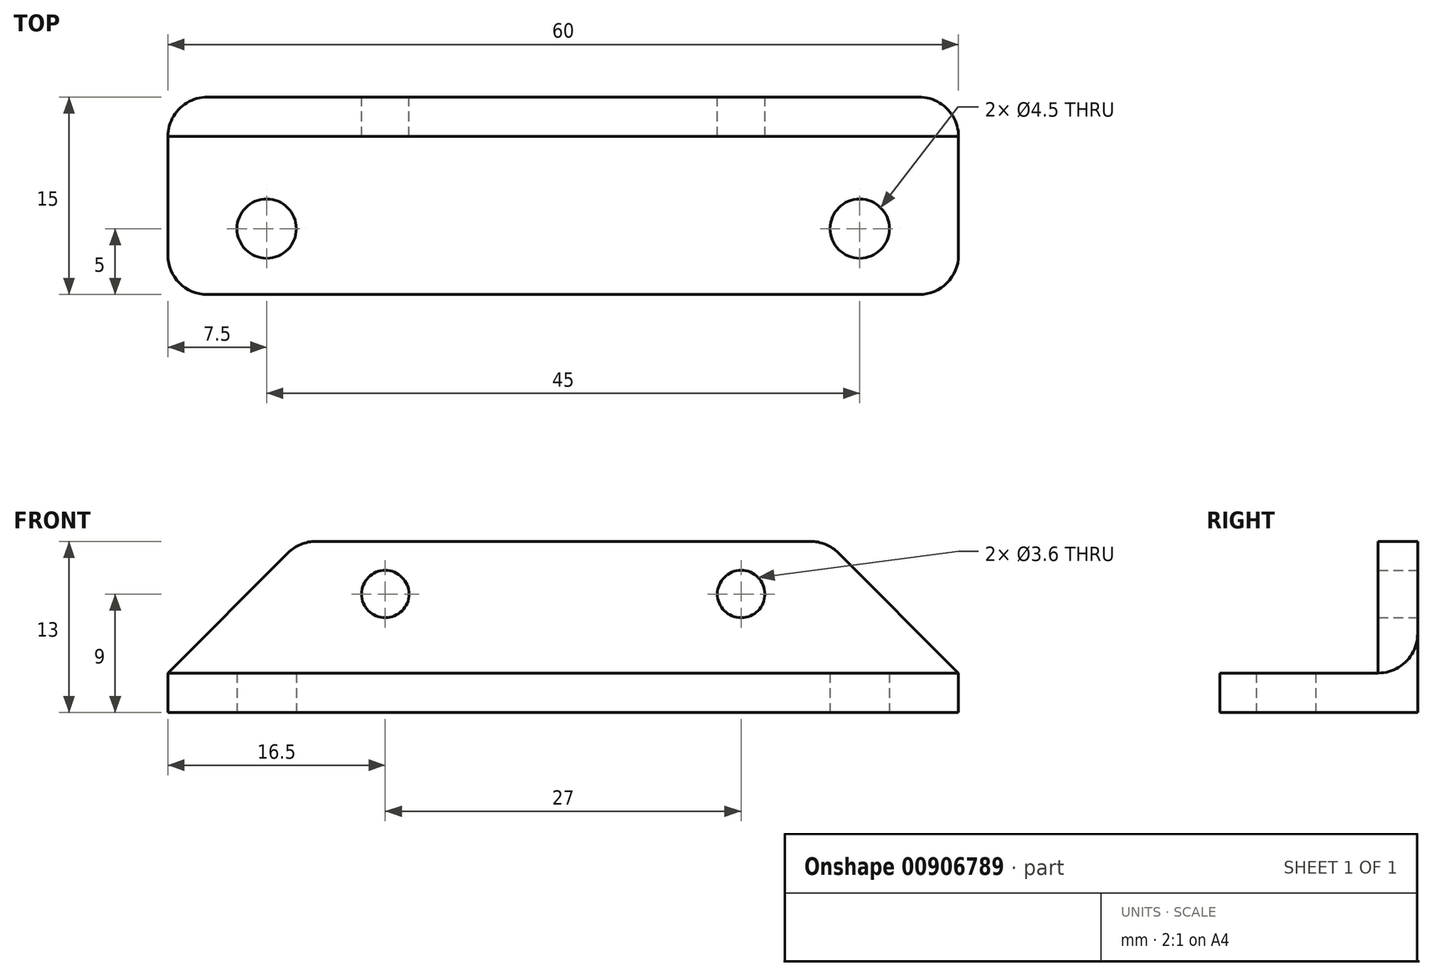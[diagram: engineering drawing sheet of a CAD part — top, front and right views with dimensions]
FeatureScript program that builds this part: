
annotation { "Feature Type Name" : "Feature", "Feature Type Description" : "" }
export const myFeature = defineFeature(function(context is Context, id is Id, definition is map)
    precondition{}
    {
        {
            var Q0;
            Q0=qCreatedBy(makeId("Top.planeOp"),FACE);
            var sketch = newSketch(context, id + "F0", { "sketchPlane" : qUnion([Q0])});
            skLineSegment(sketch, "E0.bottom", {"start": v(50, -10) * mm, "end": v(-50, -10) * mm, "construction": true});
            skLineSegment(sketch, "E0.top", {"start": v(50, 10) * mm, "end": v(-50, 10) * mm, "construction": true});
            skLineSegment(sketch, "E0.left", {"start": v(50, -10) * mm, "end": v(50, 10) * mm, "construction": true});
            skLineSegment(sketch, "E0.right", {"start": v(-50, -10) * mm, "end": v(-50, 10) * mm, "construction": true});
            skPoint(sketch, "E0.middle", {"position": v(0, 0) * mm});
            skCircle(sketch, "E1", {"center": v(-22.5, 0) * mm, "radius": 2.25 * mm});
            skCircle(sketch, "E2", {"center": v(22.5, 0) * mm, "radius": 2.25 * mm});
            skLineSegment(sketch, "E3.bottom", {"start": v(30, 10) * mm, "end": v(-30, 10) * mm});
            skLineSegment(sketch, "E3.top", {"start": v(30, -5) * mm, "end": v(-30, -5) * mm});
            skLineSegment(sketch, "E3.left", {"start": v(30, 10) * mm, "end": v(30, -5) * mm});
            skLineSegment(sketch, "E3.right", {"start": v(-30, 10) * mm, "end": v(-30, -5) * mm});
            skPoint(sketch, "E3.middle", {"position": v(0, 2.5) * mm});
            skSolve(sketch);
        }
        {
            var Q0;
            Q0=makeQuery(id+"F0.imprint","IMPRINT",FACE,{"disambiguationData":[TD([[makeQuery(id+"F0.imprint","IMPRINT",EDGE,{"derivedFrom":sQuery(id+"F0.wireOp",EDGE,"E1")}),-1.0]])]});
            extrude(context, id + "F1", {"entities" : qUnion([Q0]), "depth" : 3 * mm, "offsetDistance" : 25 * mm});
        }
        {
            var Q0;
            Q0=makeQuery(id+"F1.opExtrude","SWEPT_FACE",FACE,{"disambiguationData":[OSD([sQuery(id+"F0.wireOp",EDGE,"E3.bottom")])]});
            var sketch = newSketch(context, id + "F2", { "sketchPlane" : qUnion([Q0])});
            skPoint(sketch, "E4", {"position": v(0, 9) * mm});
            skCircle(sketch, "E5", {"center": v(-13.5, 9) * mm, "radius": 1.8 * mm});
            skCircle(sketch, "E6", {"center": v(13.5, 9) * mm, "radius": 1.8 * mm});
            skLineSegment(sketch, "E7", {"start": v(-30, 3) * mm, "end": v(-20, 13) * mm});
            skLineSegment(sketch, "E8", {"start": v(-20, 13) * mm, "end": v(20, 13) * mm});
            skLineSegment(sketch, "E9", {"start": v(20, 13) * mm, "end": v(30, 3) * mm});
            skSolve(sketch);
        }
        {
            var Q0;
            Q0=makeQuery(id+"F2.imprint","IMPRINT",FACE,{"disambiguationData":[TD([[makeQuery(id+"F2.imprint","IMPRINT",EDGE,{"derivedFrom":sQuery(id+"F2.wireOp",EDGE,"E5")}),-1.0]])]});
            extrude(context, id + "F3", {"entities" : qUnion([Q0]), "operationType" : NewBodyOperationType.ADD, "oppositeDirection" : true, "depth" : 3 * mm, "offsetDistance" : 25 * mm});
        }
        {
            var Q0;
            Q0=makeQuery(id+"F1.opExtrude","SWEPT_EDGE",EDGE,{"disambiguationData":[OSD([sQuery(id+"F0.wireOp",EDGE,"E3.top"),sQuery(id+"F0.wireOp",EDGE,"E3.right")])]});
            var Q1;
            Q1=makeQuery(id+"F1.opExtrude","SWEPT_EDGE",EDGE,{"disambiguationData":[OSD([sQuery(id+"F0.wireOp",EDGE,"E3.top"),sQuery(id+"F0.wireOp",EDGE,"E3.left")])]});
            var Q2;
            Q2=makeQuery(id+"F1.opExtrude","SWEPT_EDGE",EDGE,{"disambiguationData":[OSD([sQuery(id+"F0.wireOp",EDGE,"E3.bottom"),sQuery(id+"F0.wireOp",EDGE,"E3.left")])]});
            var Q3;
            Q3=makeQuery(id+"F1.opExtrude","SWEPT_EDGE",EDGE,{"disambiguationData":[OSD([sQuery(id+"F0.wireOp",EDGE,"E3.bottom"),sQuery(id+"F0.wireOp",EDGE,"E3.right")])]});
            var Q4;
            Q4=makeQuery(id+"F3.opExtrude","SWEPT_EDGE",EDGE,{"disambiguationData":[OSD([sQuery(id+"F2.wireOp",EDGE,"E8"),sQuery(id+"F2.wireOp",EDGE,"E9")])]});
            var Q5;
            Q5=makeQuery(id+"F3.opExtrude","SWEPT_EDGE",EDGE,{"disambiguationData":[OSD([sQuery(id+"F2.wireOp",EDGE,"E7"),sQuery(id+"F2.wireOp",EDGE,"E8")])]});
            fillet(context, id + "F4", {"entities" : qUnion([Q0, Q1, Q2, Q3, Q4, Q5]), "radius" : 3 * mm, "tangentPropagation" : true, "allowEdgeOverflow" : false});
        }
    });
